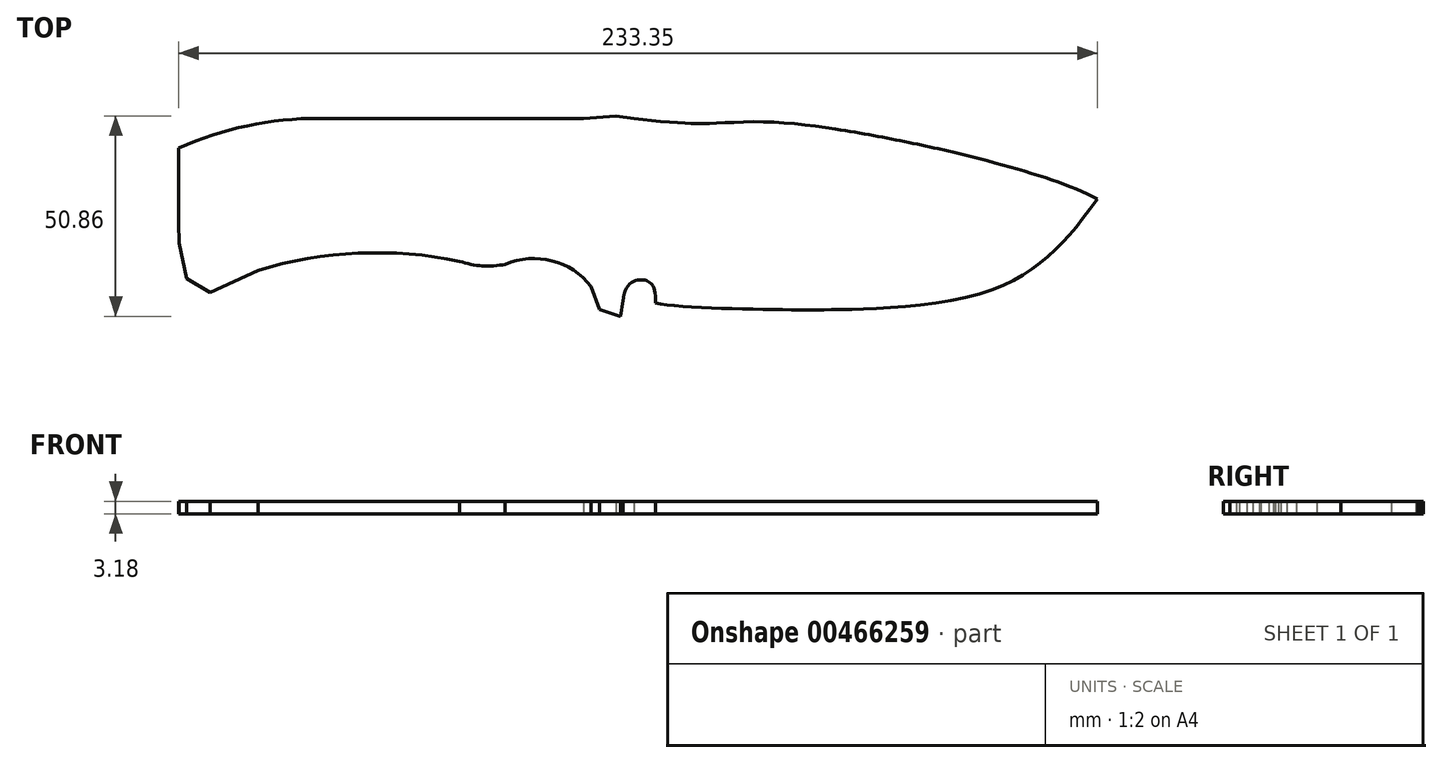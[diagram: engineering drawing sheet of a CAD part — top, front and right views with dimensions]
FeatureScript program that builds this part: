
annotation { "Feature Type Name" : "Feature", "Feature Type Description" : "" }
export const myFeature = defineFeature(function(context is Context, id is Id, definition is map)
    precondition{}
    {
        {
            var Q0;
            Q0=qCreatedBy(makeId("Top.planeOp"),FACE);
            var sketch = newSketch(context, id + "F0", { "sketchPlane" : qUnion([Q0])});
            skPoint(sketch, "E0.middle", {"position": v(0, 0) * mm});
            skLineSegment(sketch, "E1", {"start": v(-89.44, -13.25) * mm, "end": v(-101.59, -18.9) * mm});
            skLineSegment(sketch, "E2", {"start": v(-20.97, 25.4) * mm, "end": v(-6.68, 25.4) * mm});
            skLineSegment(sketch, "E3", {"start": v(-6.68, 25.4) * mm, "end": v(1.56, 25.96) * mm});
            skLineSegment(sketch, "E4", {"start": v(1.56, 25.96) * mm, "end": v(6.13, 25.4) * mm});
            skArc(sketch, "E5", {"start": v(-38.19, -10.94) * mm, "mid": v(-63.96, -8.86) * mm, "end": v(-89.44, -13.25) * mm});
            skArc(sketch, "E6", {"start": v(-38.19, -10.94) * mm, "mid": v(-32.47, -12.1) * mm, "end": v(-26.64, -11.69) * mm});
            skArc(sketch, "E7", {"start": v(-4.8, -17.33) * mm, "mid": v(-14.76, -10.8) * mm, "end": v(-26.64, -11.69) * mm});
            skLineSegment(sketch, "E8", {"start": v(-109.56, -1.15) * mm, "end": v(-109.56, 17.86) * mm});
            skLineSegment(sketch, "E9", {"start": v(-101.59, -18.9) * mm, "end": v(-107.52, -15.35) * mm});
            skLineSegment(sketch, "E10", {"start": v(-107.52, -15.35) * mm, "end": v(-109.46, -6.3) * mm});
            skLineSegment(sketch, "E11", {"start": v(-109.46, -6.3) * mm, "end": v(-109.56, -1.15) * mm});
            skLineSegment(sketch, "E12", {"start": v(3.33, -20.84) * mm, "end": v(2.62, -24.9) * mm});
            skLineSegment(sketch, "E13", {"start": v(2.62, -24.9) * mm, "end": v(-2.68, -23.14) * mm});
            skLineSegment(sketch, "E14", {"start": v(-2.68, -23.14) * mm, "end": v(-4.8, -17.33) * mm});
            skFitSpline(sketch, "E15", {"points": [v(61.43, -23.15) * mm, v(93.92, -19.24) * mm, v(111.43, -9.51) * mm, v(123.79, 4.94) * mm], "startDerivative": vector(63.45, 1.05) * mm, "endDerivative": vector(42.43, 61.06) * mm});
            skFitSpline(sketch, "E16", {"points": [v(61.43, -23.15) * mm, v(39.26, -23.15) * mm, v(11.5, -21.51) * mm], "startDerivative": vector(-37.46, -0.75) * mm, "endDerivative": vector(-27.65, 5.9) * mm});
            skFitSpline(sketch, "E17", {"points": [v(11.5, -21.51) * mm, v(10.04, -16.25) * mm, v(7.03, -15.72) * mm, v(3.33, -20.84) * mm], "startDerivative": vector(1.16, 26.25) * mm, "endDerivative": vector(-2.95, -29.52) * mm});
            skLineSegment(sketch, "E18", {"start": v(-20.97, 25.4) * mm, "end": v(-73.95, 25.4) * mm});
            skArc(sketch, "E19", {"start": v(-73.95, 25.4) * mm, "mid": v(-92.15, 23.5) * mm, "end": v(-109.56, 17.86) * mm});
            skArc(sketch, "E20", {"start": v(17.2, 13.15) * mm, "mid": v(9.64, -2.26) * mm, "end": v(3.87, -18.42) * mm});
            skFitSpline(sketch, "E21", {"points": [v(123.79, 4.94) * mm, v(100.89, 13.22) * mm, v(57.34, 22.66) * mm], "startDerivative": vector(-40, 21.49) * mm, "endDerivative": vector(-89.36, 14.44) * mm});
            skFitSpline(sketch, "E22", {"points": [v(57.34, 22.66) * mm, v(38.96, 24.51) * mm, v(25.12, 24.07) * mm, v(18.6, 24.17) * mm, v(6.13, 25.4) * mm], "startDerivative": vector(-58.63, 8.88) * mm, "endDerivative": vector(-48.67, 7.71) * mm});
            skPoint(sketch, "E23", {"position": v(83.3, 17.67) * mm});
            skFitSpline(sketch, "E24", {"points": [v(83.3, 17.67) * mm, v(74.67, 15.23) * mm, v(64.57, 15.57) * mm, v(53.54, 17.01) * mm, v(39.28, 18.62) * mm, v(27.23, 17.67) * mm, v(19.23, 14.7) * mm], "startDerivative": vector(-55.55, -20.48) * mm, "endDerivative": vector(-53.68, -24.72) * mm});
            skFitSpline(sketch, "E25", {"points": [v(19.23, 14.7) * mm, v(17.2, 13.15) * mm], "startDerivative": vector(-1.8, -0.81) * mm, "endDerivative": vector(-1.2, -1.73) * mm});
            skSolve(sketch);
        }
        {
            var Q0;
            Q0=makeQuery(id+"F0.imprint","IMPRINT",FACE,{"disambiguationData":[TD([[makeQuery(id+"F0.imprint","IMPRINT",EDGE,{"derivedFrom":sQuery(id+"F0.wireOp",EDGE,"E1")}),-1.0]])]});
            extrude(context, id + "F1", {"entities" : qUnion([Q0]), "depth" : 1.59 * mm});
        }
        {
            var Q0;
            Q0=makeQuery(id+"F1.opExtrude","CAP_FACE",FACE,{"disambiguationData":[OSD([sQuery(id+"F0.wireOp",EDGE,"E1"),sQuery(id+"F0.wireOp",EDGE,"E2"),sQuery(id+"F0.wireOp",EDGE,"E3"),sQuery(id+"F0.wireOp",EDGE,"E4"),sQuery(id+"F0.wireOp",EDGE,"E5"),sQuery(id+"F0.wireOp",EDGE,"E6"),sQuery(id+"F0.wireOp",EDGE,"E7"),sQuery(id+"F0.wireOp",EDGE,"E8"),sQuery(id+"F0.wireOp",EDGE,"E9"),sQuery(id+"F0.wireOp",EDGE,"E10"),sQuery(id+"F0.wireOp",EDGE,"E11"),sQuery(id+"F0.wireOp",EDGE,"E12"),sQuery(id+"F0.wireOp",EDGE,"E13"),sQuery(id+"F0.wireOp",EDGE,"E14"),sQuery(id+"F0.wireOp",EDGE,"E17"),sQuery(id+"F0.wireOp",EDGE,"E18"),sQuery(id+"F0.wireOp",EDGE,"E19"),sQuery(id+"F0.wireOp",EDGE,"E20"),sQuery(id+"F0.wireOp",EDGE,"E21"),sQuery(id+"F0.wireOp",EDGE,"E22"),sQuery(id+"F0.wireOp",EDGE,"E24"),sQuery(id+"F0.wireOp",EDGE,"E25")])],"isStart":true});
            extrude(context, id + "F2", {"entities" : qUnion([Q0]), "operationType" : NewBodyOperationType.ADD, "depth" : 1.59 * mm});
        }
        {
            var Q0;
            {var subQ3=sQuery(id+"F0.wireOp",EDGE,"E15");Q0=makeQuery(id+"F0.imprint","IMPRINT",FACE,{"disambiguationData":[TD([[makeQuery(id+"F0.imprint","IMPRINT",EDGE,{"derivedFrom":subQ3}),1.0]])]});}
            extrude(context, id + "F3", {"entities" : qUnion([Q0]), "operationType" : NewBodyOperationType.ADD, "depth" : 1.59 * mm, "hasSecondDirection" : true, "secondDirectionOppositeDirection" : true, "secondDirectionDepth" : 1.59 * mm});
        }
    });
